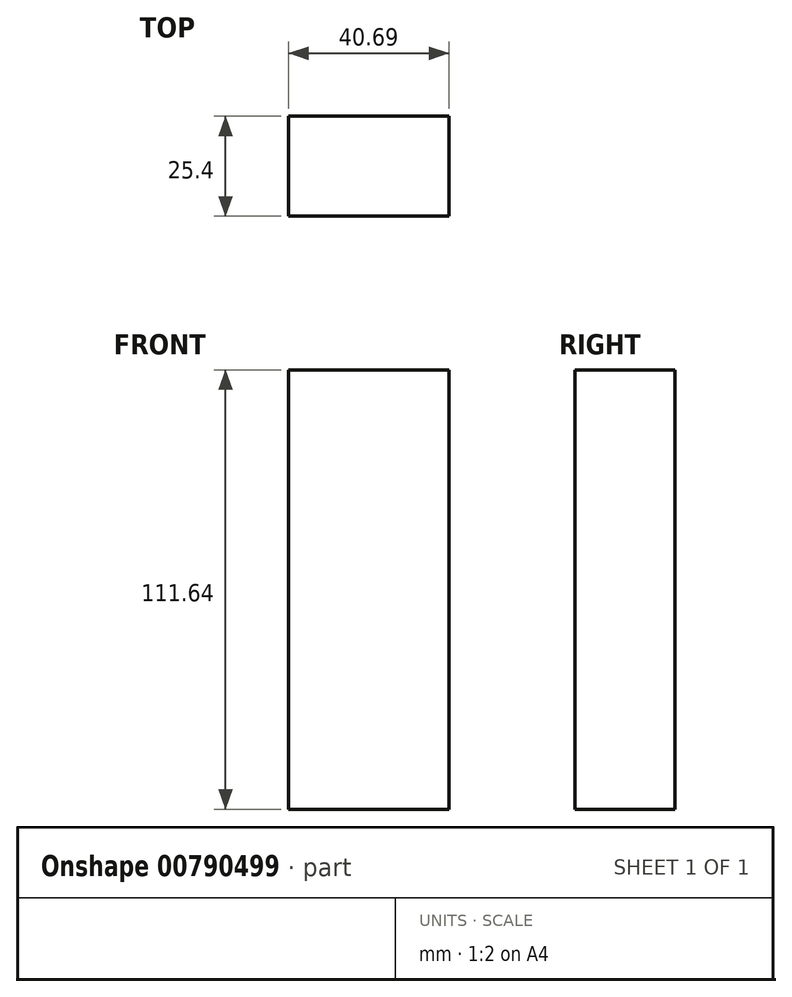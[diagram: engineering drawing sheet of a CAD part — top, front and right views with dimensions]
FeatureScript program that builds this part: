
annotation { "Feature Type Name" : "Feature", "Feature Type Description" : "" }
export const myFeature = defineFeature(function(context is Context, id is Id, definition is map)
    precondition{}
    {
        {
            var Q0;
            Q0=qCreatedBy(makeId("Front.planeOp"),FACE);
            var sketch = newSketch(context, id + "F0", { "sketchPlane" : qUnion([Q0])});
            skLineSegment(sketch, "E0.bottom", {"start": v(-82.49, -89.33) * mm, "end": v(-52.8, -89.33) * mm});
            skLineSegment(sketch, "E0.top", {"start": v(-82.49, -89.64) * mm, "end": v(-52.8, -89.64) * mm});
            skLineSegment(sketch, "E0.left", {"start": v(-82.49, -89.33) * mm, "end": v(-82.49, -89.64) * mm});
            skLineSegment(sketch, "E0.right", {"start": v(-52.8, -89.33) * mm, "end": v(-52.8, -89.64) * mm});
            skLineSegment(sketch, "E1.bottom", {"start": v(-49.31, 69.47) * mm, "end": v(-86.16, 69.47) * mm});
            skLineSegment(sketch, "E1.top", {"start": v(-49.31, 70.4) * mm, "end": v(-86.16, 70.4) * mm});
            skLineSegment(sketch, "E1.left", {"start": v(-49.31, 69.47) * mm, "end": v(-49.31, 70.4) * mm});
            skLineSegment(sketch, "E1.right", {"start": v(-86.16, 69.47) * mm, "end": v(-86.16, 70.4) * mm});
            skLineSegment(sketch, "E2", {"start": v(-86.16, 69.47) * mm, "end": v(-82.49, -89.33) * mm});
            skLineSegment(sketch, "E3", {"start": v(-48.03, 68.92) * mm, "end": v(-52.8, -89.33) * mm});
            skLineSegment(sketch, "E4.bottom", {"start": v(0, 0) * mm, "end": v(0, 0) * mm});
            skLineSegment(sketch, "E4.top", {"start": v(0, 0) * mm, "end": v(0, 0) * mm});
            skLineSegment(sketch, "E4.left", {"start": v(0, 0) * mm, "end": v(0, 0) * mm});
            skLineSegment(sketch, "E4.right", {"start": v(0, 0) * mm, "end": v(0, 0) * mm});
            skPoint(sketch, "E4.middle", {"position": v(0, 0) * mm});
            skLineSegment(sketch, "E5.bottom", {"start": v(-24.38, -61.6) * mm, "end": v(16.31, -61.6) * mm});
            skLineSegment(sketch, "E5.top", {"start": v(-24.38, 61.23) * mm, "end": v(16.31, 61.23) * mm});
            skLineSegment(sketch, "E5.left", {"start": v(-24.38, -61.6) * mm, "end": v(-24.38, 61.23) * mm});
            skLineSegment(sketch, "E5.right", {"start": v(16.31, -61.6) * mm, "end": v(16.31, 61.23) * mm});
            skPoint(sketch, "E5.middle", {"position": v(-4.03, -0.18) * mm});
            skLineSegment(sketch, "E6.0", {"start": v(-24.38, 56.4) * mm, "end": v(16.31, 56.4) * mm});
            skLineSegment(sketch, "E7.0", {"start": v(-24.38, 50.05) * mm, "end": v(16.31, 50.05) * mm});
            skSolve(sketch);
        }
        {
            var Q0;
            {var subQ0=sQuery(id+"F0.wireOp",EDGE,"E5.bottom");Q0=makeQuery(id+"F0.imprint","IMPRINT",FACE,{"disambiguationData":[TD([[makeQuery(id+"F0.imprint","IMPRINT",EDGE,{"derivedFrom":subQ0}),1.0]])]});}
            extrude(context, id + "F1", {"entities" : qUnion([Q0]), "depth" : 25.4 * mm, "offsetDistance" : 25.4 * mm});
        }
    });
